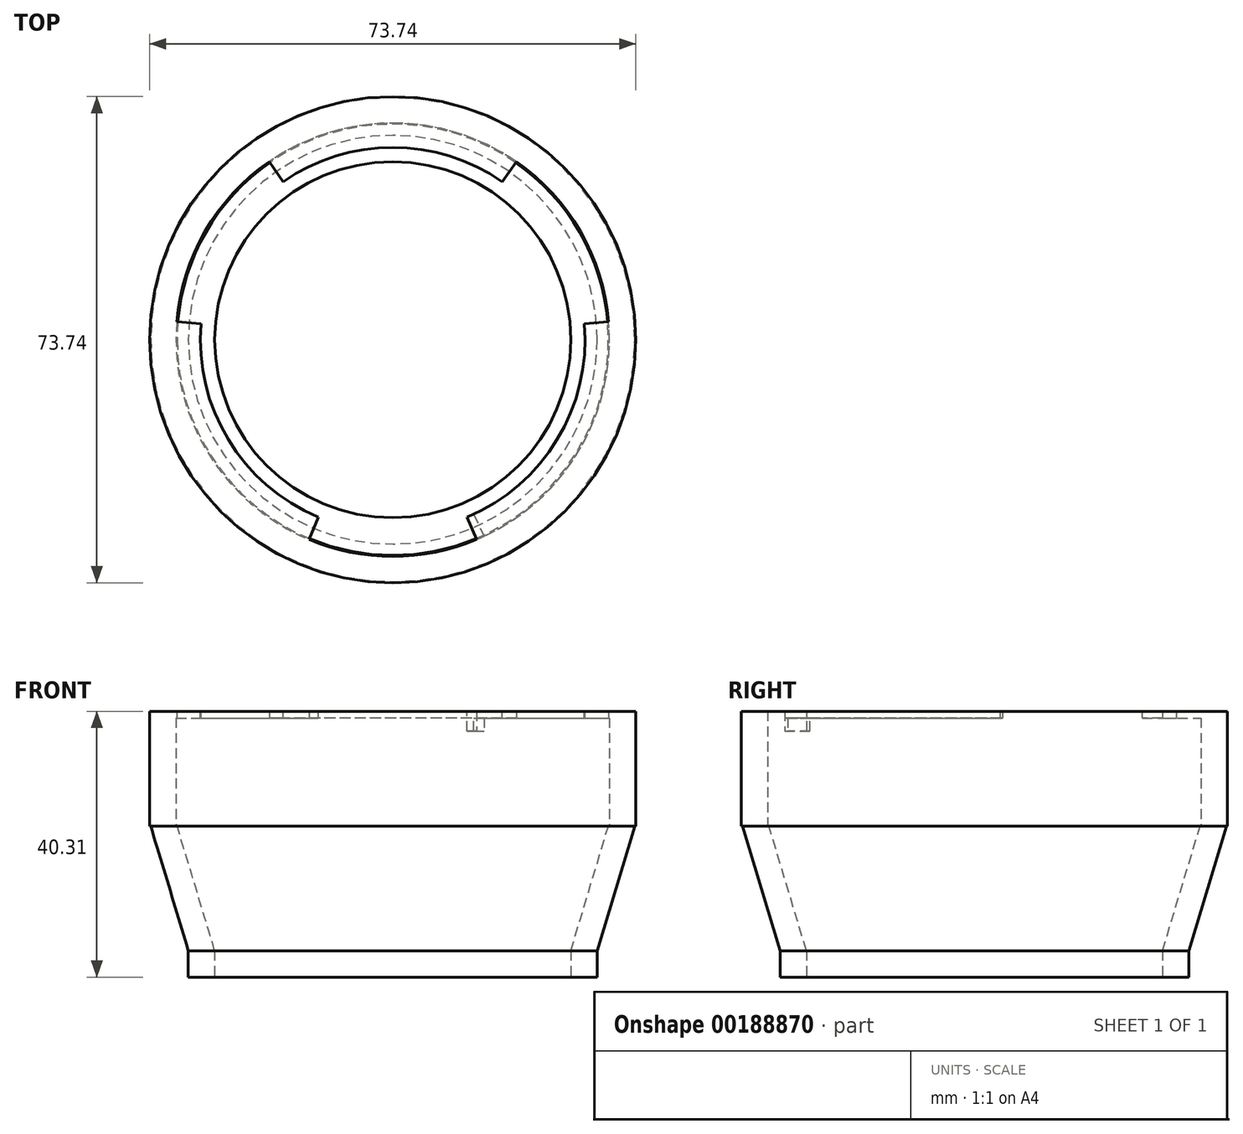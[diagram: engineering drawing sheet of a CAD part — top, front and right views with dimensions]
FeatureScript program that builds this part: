
annotation { "Feature Type Name" : "Feature", "Feature Type Description" : "" }
export const myFeature = defineFeature(function(context is Context, id is Id, definition is map)
    precondition{}
    {
        {
            var Q0;
            Q0=qCreatedBy(makeId("Top.planeOp"),FACE);
            var sketch = newSketch(context, id + "F10", { "sketchPlane" : qUnion([Q0]), "disableImprinting" : false});
            skCircle(sketch, "E0", {"center": v(0, 0) * mm, "radius": 27 * mm});
            skCircle(sketch, "E1", {"center": v(0, 0) * mm, "radius": 31 * mm});
            skSolve(sketch);
        }
        {
            var Q0;
            Q0=qCreatedBy(makeId("Front.planeOp"),FACE);
            var sketch = newSketch(context, id + "F0", { "sketchPlane" : qUnion([Q0]), "disableImprinting" : false});
            skLineSegment(sketch, "E2", {"start": v(-32.7, 22.92) * mm, "end": v(-36.7, 22.92) * mm});
            skLineSegment(sketch, "E3", {"start": v(-31, 4) * mm, "end": v(-27, 4) * mm});
            skLineSegment(sketch, "E4", {"start": v(-36.7, 22.92) * mm, "end": v(-31, 4) * mm});
            skLineSegment(sketch, "E5", {"start": v(-32.7, 22.92) * mm, "end": v(-27, 4) * mm});
            skSolve(sketch);
        }
        {
            var Q0;
            Q0=makeQuery(id+"F10.imprint","IMPRINT",FACE,{"disambiguationData":[TD([[makeQuery(id+"F10.imprint","IMPRINT",EDGE,{"derivedFrom":sQuery(id+"F10.wireOp",EDGE,"E0")}),-1.0]])]});
            extrude(context, id + "F1", {"entities" : qUnion([Q0]), "depth" : 4 * mm});
        }
        {
            var Q0;
            Q0=qCreatedBy(makeId("Top.planeOp"),FACE);
            cPlane(context, id + "F2", {"entities" : qUnion([Q0]), "cplaneType" : CPlaneType.OFFSET, "offset" : 22.92 * mm, "width" : 150 * mm, "height" : 150 * mm});
        }
        {
            var Q0;
            Q0=qCreatedBy(id+"F2.planeOp",FACE);
            var sketch = newSketch(context, id + "F3", { "sketchPlane" : qUnion([Q0])});
            skCircle(sketch, "E6", {"center": v(0, 0) * mm, "radius": 32.87 * mm});
            skCircle(sketch, "E7", {"center": v(0, 0) * mm, "radius": 36.87 * mm});
            skSolve(sketch);
        }
        {
            var Q0;
            Q0=makeQuery(id+"F3.imprint","IMPRINT",FACE,{"disambiguationData":[TD([[makeQuery(id+"F3.imprint","IMPRINT",EDGE,{"derivedFrom":sQuery(id+"F3.wireOp",EDGE,"E6")}),-1.0]])]});
            extrude(context, id + "F4", {"entities" : qUnion([Q0]), "depth" : 17.4 * mm});
        }
        {
            var Q0;
            Q0=qCreatedBy(makeId("Top.planeOp"),FACE);
            cPlane(context, id + "F5", {"entities" : qUnion([Q0]), "cplaneType" : CPlaneType.OFFSET, "offset" : 40.31 * mm, "width" : 150 * mm, "height" : 150 * mm});
        }
        {
            var Q0;
            Q0=qCreatedBy(id+"F5.planeOp",FACE);
            var sketch = newSketch(context, id + "F6", { "sketchPlane" : qUnion([Q0])});
            skCircle(sketch, "E8", {"center": v(0, 0) * mm, "radius": 32.97 * mm});
            skCircle(sketch, "E9", {"center": v(0, 0) * mm, "radius": 36.87 * mm});
            skLineSegment(sketch, "E10", {"start": v(0, -32.97) * mm, "end": v(0, -29.17) * mm});
            skLineSegment(sketch, "E11", {"start": v(0, -29.17) * mm, "end": v(-12.7, -29.17) * mm});
            skLineSegment(sketch, "E12", {"start": v(0, -29.17) * mm, "end": v(12.7, -29.17) * mm});
            skArc(sketch, "E13", {"start": v(-12.74, -30.4) * mm, "mid": v(0, -32.97) * mm, "end": v(12.74, -30.4) * mm});
            skLineSegment(sketch, "E14", {"start": v(-12.74, -30.4) * mm, "end": v(-11.28, -26.9) * mm});
            skLineSegment(sketch, "E15", {"start": v(12.74, -30.4) * mm, "end": v(11.28, -26.9) * mm});
            skArc(sketch, "E16", {"start": v(-11.28, -26.9) * mm, "mid": v(0, -29.17) * mm, "end": v(11.28, -26.9) * mm});
            skLineSegment(sketch, "E17", {"start": v(25.26, 14.59) * mm, "end": v(28.55, 16.48) * mm});
            skLineSegment(sketch, "E18", {"start": v(-25.26, 14.59) * mm, "end": v(-28.55, 16.48) * mm});
            skLineSegment(sketch, "E19", {"start": v(28.55, 16.48) * mm, "end": v(35.56, 4.34) * mm});
            skLineSegment(sketch, "E20", {"start": v(28.55, 16.48) * mm, "end": v(21.54, 28.62) * mm});
            skArc(sketch, "E21", {"start": v(18.79, 27.09) * mm, "mid": v(28.55, 16.48) * mm, "end": v(32.85, 2.73) * mm});
            skLineSegment(sketch, "E22", {"start": v(18.79, 27.09) * mm, "end": v(16.63, 23.97) * mm});
            skLineSegment(sketch, "E23", {"start": v(29.07, 2.41) * mm, "end": v(32.85, 2.73) * mm});
            skArc(sketch, "E24", {"start": v(16.63, 23.97) * mm, "mid": v(25.26, 14.59) * mm, "end": v(29.07, 2.41) * mm});
            skPoint(sketch, "E25.orphan", {"position": v(0, -36.87) * mm});
            skLineSegment(sketch, "E26", {"start": v(-28.55, 16.48) * mm, "end": v(-35.56, 4.34) * mm});
            skLineSegment(sketch, "E27", {"start": v(-28.55, 16.48) * mm, "end": v(-21.54, 28.62) * mm});
            skArc(sketch, "E28", {"start": v(-16.63, 23.97) * mm, "mid": v(-25.26, 14.59) * mm, "end": v(-29.07, 2.41) * mm});
            skArc(sketch, "E29", {"start": v(-32.85, 2.73) * mm, "mid": v(-28.55, 16.48) * mm, "end": v(-18.79, 27.09) * mm});
            skLineSegment(sketch, "E30", {"start": v(-32.85, 2.73) * mm, "end": v(-29.07, 2.41) * mm});
            skLineSegment(sketch, "E31", {"start": v(-16.63, 23.97) * mm, "end": v(-18.79, 27.09) * mm});
            skCircle(sketch, "E32", {"center": v(0, 0) * mm, "radius": 29.17 * mm});
            skLineSegment(sketch, "E33", {"start": v(12.3, -26.46) * mm, "end": v(13.89, -29.9) * mm});
            skSolve(sketch);
        }
        {
            var Q0;
            Q0 = qSketchRegion(id + "F0", true);
            var Q1;
            Q1=makeQuery(id+"F1.opExtrude","CAP_EDGE",EDGE,{"disambiguationData":[OSD([sQuery(id+"F10.wireOp",EDGE,"E0")])],"isStart":false});
            sweep(context, id + "F7", {"profiles" : qUnion([Q0]), "path" : qUnion([Q1])});
        }
        {
            var Q0;
            {var subQ0=sQuery(id+"F6.wireOp",EDGE,"E30");Q0=makeQuery(id+"F6.imprint","IMPRINT",FACE,{"disambiguationData":[TD([[makeQuery(id+"F6.imprint","IMPRINT",EDGE,{"derivedFrom":subQ0}),-1.0]])]});}
            var Q1;
            {var subQ0=sQuery(id+"F6.wireOp",EDGE,"E22");Q1=makeQuery(id+"F6.imprint","IMPRINT",FACE,{"disambiguationData":[TD([[makeQuery(id+"F6.imprint","IMPRINT",EDGE,{"derivedFrom":subQ0}),-1.0]])]});}
            var Q2;
            {var subQ0=sQuery(id+"F6.wireOp",EDGE,"E23");Q2=makeQuery(id+"F6.imprint","IMPRINT",FACE,{"disambiguationData":[TD([[makeQuery(id+"F6.imprint","IMPRINT",EDGE,{"derivedFrom":subQ0}),-1.0]])]});}
            extrude(context, id + "F8", {"entities" : qUnion([Q0, Q1, Q2]), "operationType" : NewBodyOperationType.ADD, "oppositeDirection" : true, "depth" : 1 * mm});
        }
        {
            var Q0;
            {var subQ3=sQuery(id+"F6.wireOp",EDGE,"E33");Q0=makeQuery(id+"F6.imprint","IMPRINT",FACE,{"disambiguationData":[TD([[makeQuery(id+"F6.imprint","IMPRINT",EDGE,{"derivedFrom":subQ3}),-1.0]])]});}
            extrude(context, id + "F9", {"entities" : qUnion([Q0]), "operationType" : NewBodyOperationType.ADD, "oppositeDirection" : true, "depth" : 3 * mm});
        }
    });
